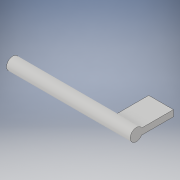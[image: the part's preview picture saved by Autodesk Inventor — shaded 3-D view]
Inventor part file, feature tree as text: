
AUTODESK INVENTOR PART (.ipt)
format: ipt  version: 2017 (Build 210142000, 142)  size: 110,592 bytes
history: native  units: in
note: dims shown in document units (in); Inventor stores cm internally (conversion verified against a paired STEP export)
features: extrude x2, sketch x2, projected_geometry x1
ambient origin geometry x8: Origin, YZ Plane, XZ Plane, XY Plane, X Axis, Y Axis, Z Axis, Center Point
bodies: Solid1 (feature_tree)
feature tree (5):
  extrude  "Extrusion1"  Depth=5.0in TaperAngle=0.0deg
  extrude  "Extrusion2"  Depth=0.25in
  sketch  "Sketch1"  dims[d0=0.5in d1=5.0in d2=0.0in]
  sketch  "Sketch2"  dims[d3=0.5in d4=0.25in d5=0.125in d6=1.5in d7=0.0in d8=1.0in d9=0.0in]
  projected_geometry  "Projected Loop1"
